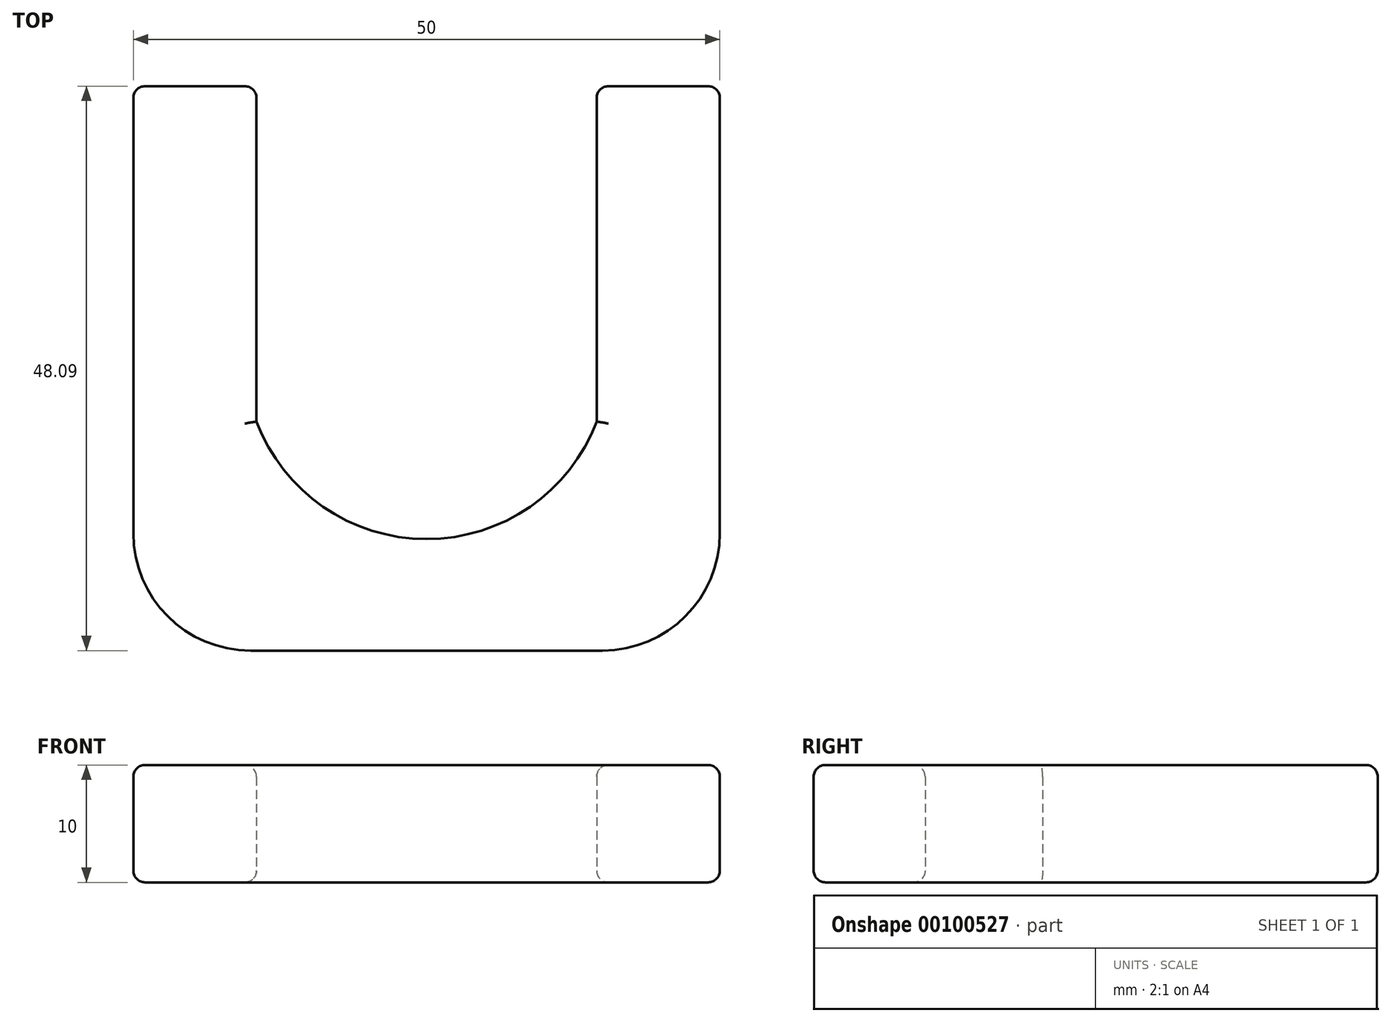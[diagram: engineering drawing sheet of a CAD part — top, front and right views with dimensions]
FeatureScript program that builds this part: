
annotation { "Feature Type Name" : "Feature", "Feature Type Description" : "" }
export const myFeature = defineFeature(function(context is Context, id is Id, definition is map)
    precondition{}
    {
        {
            var Q0;
            Q0=qCreatedBy(makeId("Top.planeOp"),FACE);
            var sketch = newSketch(context, id + "F0", { "sketchPlane" : qUnion([Q0])});
            skArc(sketch, "E0", {"start": v(-14.5, -5.48) * mm, "mid": v(0, -15.5) * mm, "end": v(14.5, -5.48) * mm});
            skLineSegment(sketch, "E1", {"start": v(-14.5, -5.48) * mm, "end": v(-14.5, 23.09) * mm});
            skLineSegment(sketch, "E2", {"start": v(-14.5, 23.09) * mm, "end": v(-25, 23.09) * mm});
            skLineSegment(sketch, "E3", {"start": v(-25, 23.09) * mm, "end": v(-25, -25) * mm});
            skLineSegment(sketch, "E4", {"start": v(-25, -25) * mm, "end": v(0, -25) * mm});
            skLineSegment(sketch, "E5.MirrorCS", {"start": v(14.5, -5.48) * mm, "end": v(14.5, 23.09) * mm});
            skLineSegment(sketch, "E6.MirrorCS", {"start": v(14.5, 23.09) * mm, "end": v(25, 23.09) * mm});
            skLineSegment(sketch, "E7.MirrorCS", {"start": v(25, 23.09) * mm, "end": v(25, -25) * mm});
            skLineSegment(sketch, "E8.MirrorCS", {"start": v(25, -25) * mm, "end": v(0, -25) * mm});
            skPoint(sketch, "E9.start.orphan", {"position": v(0, -15.5) * mm});
            skPoint(sketch, "E10.orphan", {"position": v(-14.5, -15.5) * mm});
            skPoint(sketch, "E11.orphan", {"position": v(14.5, -15.5) * mm});
            skSolve(sketch);
        }
        {
            var Q0;
            Q0=makeQuery(id+"F0.imprint","IMPRINT",FACE,{"disambiguationData":[TD([[makeQuery(id+"F0.imprint","IMPRINT",EDGE,{"derivedFrom":sQuery(id+"F0.wireOp",EDGE,"E0")}),-1.0]])]});
            extrude(context, id + "F1", {"entities" : qUnion([Q0]), "depth" : 10 * mm});
        }
        {
            var Q0;
            Q0=makeQuery(id+"F1.opExtrude","SWEPT_EDGE",EDGE,{"disambiguationData":[OSD([sQuery(id+"F0.wireOp",EDGE,"E3"),sQuery(id+"F0.wireOp",EDGE,"E4")])]});
            var Q1;
            Q1=makeQuery(id+"F1.opExtrude","SWEPT_EDGE",EDGE,{"disambiguationData":[OSD([sQuery(id+"F0.wireOp",EDGE,"E7.MirrorCS"),sQuery(id+"F0.wireOp",EDGE,"E8.MirrorCS")])]});
            fillet(context, id + "F2", {"entities" : qUnion([Q0, Q1]), "radius" : 10 * mm, "tangentPropagation" : true, "allowEdgeOverflow" : false});
        }
        {
            var Q0;
            Q0=makeQuery(id+"F1.opExtrude","CAP_EDGE",EDGE,{"disambiguationData":[OSD([sQuery(id+"F0.wireOp",EDGE,"E4"),sQuery(id+"F0.wireOp",EDGE,"E8.MirrorCS")])],"isStart":true});
            var Q1;
            Q1=makeQuery(id+"F1.opExtrude","CAP_EDGE",EDGE,{"disambiguationData":[OSD([sQuery(id+"F0.wireOp",EDGE,"E4"),sQuery(id+"F0.wireOp",EDGE,"E8.MirrorCS")])],"isStart":false});
            var Q2;
            {var subQ0=sQuery(id+"F0.wireOp",EDGE,"E8.MirrorCS");var subQ1=sQuery(id+"F0.wireOp",EDGE,"E7.MirrorCS");Q2=makeQuery(id+"F2.opFillet","BLEND_EDGE",EDGE,{"blendedFrom":[makeQuery(id+"F1.opExtrude","SWEPT_EDGE",EDGE,{"disambiguationData":[OSD([subQ1,subQ0])]}),makeQuery(id+"F1.opExtrude","CAP_FACE",FACE,{"disambiguationData":[OSD([sQuery(id+"F0.wireOp",EDGE,"E0"),sQuery(id+"F0.wireOp",EDGE,"E1"),sQuery(id+"F0.wireOp",EDGE,"E2"),sQuery(id+"F0.wireOp",EDGE,"E3"),sQuery(id+"F0.wireOp",EDGE,"E4"),sQuery(id+"F0.wireOp",EDGE,"E5.MirrorCS"),sQuery(id+"F0.wireOp",EDGE,"E6.MirrorCS"),subQ1,subQ0])],"isStart":true})],"blendedInto":[makeQuery(id+"F1.opExtrude","CAP_FACE",FACE,{"disambiguationData":[OSD([sQuery(id+"F0.wireOp",EDGE,"E0"),sQuery(id+"F0.wireOp",EDGE,"E1"),sQuery(id+"F0.wireOp",EDGE,"E2"),sQuery(id+"F0.wireOp",EDGE,"E3"),sQuery(id+"F0.wireOp",EDGE,"E4"),sQuery(id+"F0.wireOp",EDGE,"E5.MirrorCS"),sQuery(id+"F0.wireOp",EDGE,"E6.MirrorCS"),subQ1,subQ0])],"isStart":true})]});}
            var Q3;
            {var subQ0=sQuery(id+"F0.wireOp",EDGE,"E8.MirrorCS");var subQ1=sQuery(id+"F0.wireOp",EDGE,"E7.MirrorCS");Q3=makeQuery(id+"F2.opFillet","BLEND_EDGE",EDGE,{"blendedFrom":[makeQuery(id+"F1.opExtrude","SWEPT_EDGE",EDGE,{"disambiguationData":[OSD([subQ1,subQ0])]}),makeQuery(id+"F1.opExtrude","CAP_FACE",FACE,{"disambiguationData":[OSD([sQuery(id+"F0.wireOp",EDGE,"E0"),sQuery(id+"F0.wireOp",EDGE,"E1"),sQuery(id+"F0.wireOp",EDGE,"E2"),sQuery(id+"F0.wireOp",EDGE,"E3"),sQuery(id+"F0.wireOp",EDGE,"E4"),sQuery(id+"F0.wireOp",EDGE,"E5.MirrorCS"),sQuery(id+"F0.wireOp",EDGE,"E6.MirrorCS"),subQ1,subQ0])],"isStart":false})],"blendedInto":[makeQuery(id+"F1.opExtrude","CAP_FACE",FACE,{"disambiguationData":[OSD([sQuery(id+"F0.wireOp",EDGE,"E0"),sQuery(id+"F0.wireOp",EDGE,"E1"),sQuery(id+"F0.wireOp",EDGE,"E2"),sQuery(id+"F0.wireOp",EDGE,"E3"),sQuery(id+"F0.wireOp",EDGE,"E4"),sQuery(id+"F0.wireOp",EDGE,"E5.MirrorCS"),sQuery(id+"F0.wireOp",EDGE,"E6.MirrorCS"),subQ1,subQ0])],"isStart":false})]});}
            var Q4;
            Q4=makeQuery(id+"F1.opExtrude","CAP_EDGE",EDGE,{"disambiguationData":[OSD([sQuery(id+"F0.wireOp",EDGE,"E7.MirrorCS")])],"isStart":true});
            var Q5;
            Q5=makeQuery(id+"F1.opExtrude","CAP_EDGE",EDGE,{"disambiguationData":[OSD([sQuery(id+"F0.wireOp",EDGE,"E6.MirrorCS")])],"isStart":true});
            var Q6;
            Q6=makeQuery(id+"F1.opExtrude","CAP_EDGE",EDGE,{"disambiguationData":[OSD([sQuery(id+"F0.wireOp",EDGE,"E0")])],"isStart":true});
            var Q7;
            Q7=makeQuery(id+"F1.opExtrude","CAP_EDGE",EDGE,{"disambiguationData":[OSD([sQuery(id+"F0.wireOp",EDGE,"E5.MirrorCS")])],"isStart":true});
            var Q8;
            Q8=makeQuery(id+"F1.opExtrude","CAP_EDGE",EDGE,{"disambiguationData":[OSD([sQuery(id+"F0.wireOp",EDGE,"E5.MirrorCS")])],"isStart":false});
            var Q9;
            Q9=makeQuery(id+"F1.opExtrude","CAP_EDGE",EDGE,{"disambiguationData":[OSD([sQuery(id+"F0.wireOp",EDGE,"E1")])],"isStart":true});
            var Q10;
            Q10=makeQuery(id+"F1.opExtrude","SWEPT_EDGE",EDGE,{"disambiguationData":[OSD([sQuery(id+"F0.wireOp",EDGE,"E5.MirrorCS"),sQuery(id+"F0.wireOp",EDGE,"E6.MirrorCS")])]});
            var Q11;
            Q11=makeQuery(id+"F1.opExtrude","CAP_EDGE",EDGE,{"disambiguationData":[OSD([sQuery(id+"F0.wireOp",EDGE,"E2")])],"isStart":true});
            var Q12;
            Q12=makeQuery(id+"F1.opExtrude","SWEPT_EDGE",EDGE,{"disambiguationData":[OSD([sQuery(id+"F0.wireOp",EDGE,"E2"),sQuery(id+"F0.wireOp",EDGE,"E3")])]});
            var Q13;
            {var subQ0=sQuery(id+"F0.wireOp",EDGE,"E4");var subQ1=sQuery(id+"F0.wireOp",EDGE,"E3");Q13=makeQuery(id+"F2.opFillet","BLEND_EDGE",EDGE,{"blendedFrom":[makeQuery(id+"F1.opExtrude","SWEPT_EDGE",EDGE,{"disambiguationData":[OSD([subQ1,subQ0])]}),makeQuery(id+"F1.opExtrude","CAP_FACE",FACE,{"disambiguationData":[OSD([sQuery(id+"F0.wireOp",EDGE,"E0"),sQuery(id+"F0.wireOp",EDGE,"E1"),sQuery(id+"F0.wireOp",EDGE,"E2"),subQ1,subQ0,sQuery(id+"F0.wireOp",EDGE,"E5.MirrorCS"),sQuery(id+"F0.wireOp",EDGE,"E6.MirrorCS"),sQuery(id+"F0.wireOp",EDGE,"E7.MirrorCS"),sQuery(id+"F0.wireOp",EDGE,"E8.MirrorCS")])],"isStart":false})],"blendedInto":[makeQuery(id+"F1.opExtrude","CAP_FACE",FACE,{"disambiguationData":[OSD([sQuery(id+"F0.wireOp",EDGE,"E0"),sQuery(id+"F0.wireOp",EDGE,"E1"),sQuery(id+"F0.wireOp",EDGE,"E2"),subQ1,subQ0,sQuery(id+"F0.wireOp",EDGE,"E5.MirrorCS"),sQuery(id+"F0.wireOp",EDGE,"E6.MirrorCS"),sQuery(id+"F0.wireOp",EDGE,"E7.MirrorCS"),sQuery(id+"F0.wireOp",EDGE,"E8.MirrorCS")])],"isStart":false})]});}
            var Q14;
            Q14=makeQuery(id+"F1.opExtrude","CAP_EDGE",EDGE,{"disambiguationData":[OSD([sQuery(id+"F0.wireOp",EDGE,"E3")])],"isStart":false});
            var Q15;
            Q15=makeQuery(id+"F1.opExtrude","CAP_EDGE",EDGE,{"disambiguationData":[OSD([sQuery(id+"F0.wireOp",EDGE,"E3")])],"isStart":true});
            var Q16;
            {var subQ0=sQuery(id+"F0.wireOp",EDGE,"E4");var subQ1=sQuery(id+"F0.wireOp",EDGE,"E3");Q16=makeQuery(id+"F2.opFillet","BLEND_EDGE",EDGE,{"blendedFrom":[makeQuery(id+"F1.opExtrude","SWEPT_EDGE",EDGE,{"disambiguationData":[OSD([subQ1,subQ0])]}),makeQuery(id+"F1.opExtrude","CAP_FACE",FACE,{"disambiguationData":[OSD([sQuery(id+"F0.wireOp",EDGE,"E0"),sQuery(id+"F0.wireOp",EDGE,"E1"),sQuery(id+"F0.wireOp",EDGE,"E2"),subQ1,subQ0,sQuery(id+"F0.wireOp",EDGE,"E5.MirrorCS"),sQuery(id+"F0.wireOp",EDGE,"E6.MirrorCS"),sQuery(id+"F0.wireOp",EDGE,"E7.MirrorCS"),sQuery(id+"F0.wireOp",EDGE,"E8.MirrorCS")])],"isStart":true})],"blendedInto":[makeQuery(id+"F1.opExtrude","CAP_FACE",FACE,{"disambiguationData":[OSD([sQuery(id+"F0.wireOp",EDGE,"E0"),sQuery(id+"F0.wireOp",EDGE,"E1"),sQuery(id+"F0.wireOp",EDGE,"E2"),subQ1,subQ0,sQuery(id+"F0.wireOp",EDGE,"E5.MirrorCS"),sQuery(id+"F0.wireOp",EDGE,"E6.MirrorCS"),sQuery(id+"F0.wireOp",EDGE,"E7.MirrorCS"),sQuery(id+"F0.wireOp",EDGE,"E8.MirrorCS")])],"isStart":true})]});}
            var Q17;
            Q17=makeQuery(id+"F1.opExtrude","CAP_EDGE",EDGE,{"disambiguationData":[OSD([sQuery(id+"F0.wireOp",EDGE,"E7.MirrorCS")])],"isStart":false});
            var Q18;
            Q18=makeQuery(id+"F1.opExtrude","SWEPT_EDGE",EDGE,{"disambiguationData":[OSD([sQuery(id+"F0.wireOp",EDGE,"E6.MirrorCS"),sQuery(id+"F0.wireOp",EDGE,"E7.MirrorCS")])]});
            var Q19;
            Q19=makeQuery(id+"F1.opExtrude","CAP_EDGE",EDGE,{"disambiguationData":[OSD([sQuery(id+"F0.wireOp",EDGE,"E6.MirrorCS")])],"isStart":false});
            var Q20;
            Q20=makeQuery(id+"F1.opExtrude","SWEPT_EDGE",EDGE,{"disambiguationData":[OSD([sQuery(id+"F0.wireOp",EDGE,"E1"),sQuery(id+"F0.wireOp",EDGE,"E2")])]});
            var Q21;
            Q21=makeQuery(id+"F1.opExtrude","CAP_EDGE",EDGE,{"disambiguationData":[OSD([sQuery(id+"F0.wireOp",EDGE,"E2")])],"isStart":false});
            var Q22;
            Q22=makeQuery(id+"F1.opExtrude","CAP_EDGE",EDGE,{"disambiguationData":[OSD([sQuery(id+"F0.wireOp",EDGE,"E1")])],"isStart":false});
            var Q23;
            Q23=makeQuery(id+"F1.opExtrude","CAP_EDGE",EDGE,{"disambiguationData":[OSD([sQuery(id+"F0.wireOp",EDGE,"E0")])],"isStart":false});
            fillet(context, id + "F3", {"entities" : qUnion([Q0, Q1, Q2, Q3, Q4, Q5, Q6, Q7, Q8, Q9, Q10, Q11, Q12, Q13, Q14, Q15, Q16, Q17, Q18, Q19, Q20, Q21, Q22, Q23]), "radius" : 1 * mm, "tangentPropagation" : true, "allowEdgeOverflow" : false});
        }
    });
